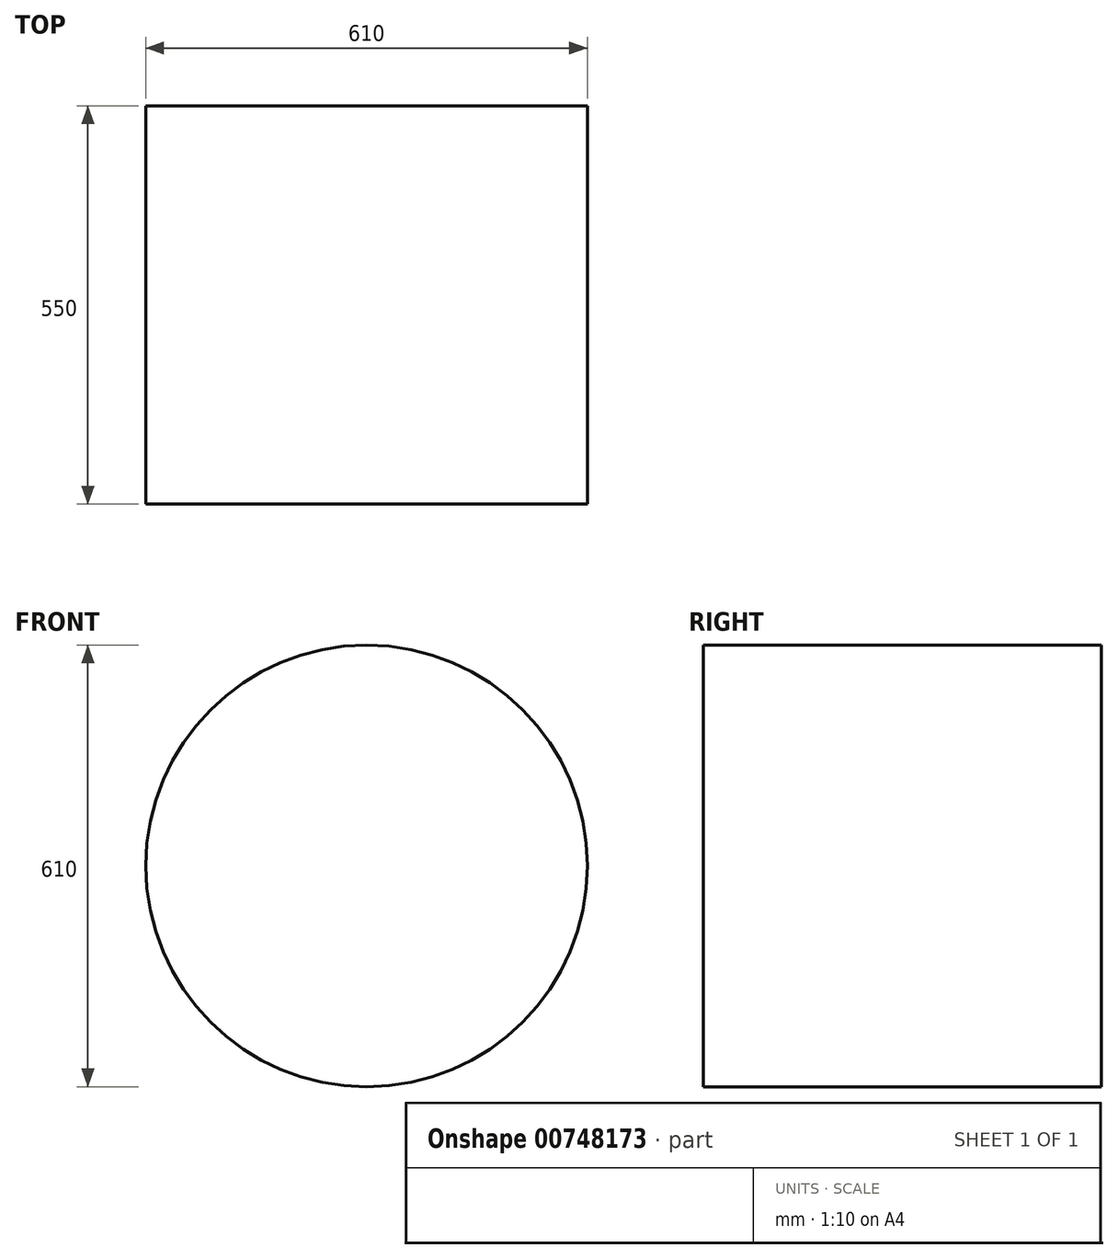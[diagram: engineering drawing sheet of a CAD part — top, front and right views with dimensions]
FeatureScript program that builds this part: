
annotation { "Feature Type Name" : "Feature", "Feature Type Description" : "" }
export const myFeature = defineFeature(function(context is Context, id is Id, definition is map)
    precondition{}
    {
        {
            var Q0;
            Q0=qCreatedBy(makeId("Front.planeOp"),FACE);
            var sketch = newSketch(context, id + "F0", { "sketchPlane" : qUnion([Q0])});
            skCircle(sketch, "E0", {"center": v(0, 0) * mm, "radius": 305 * mm});
            skSolve(sketch);
        }
        {
            var Q0;
            Q0=makeQuery(id+"F0.imprint","IMPRINT",FACE,{"disambiguationData":[TD([[makeQuery(id+"F0.imprint","IMPRINT",EDGE,{"derivedFrom":sQuery(id+"F0.wireOp",EDGE,"E0")}),1.0]])]});
            extrude(context, id + "F1", {"entities" : qUnion([Q0]), "depth" : 550 * mm, "offsetDistance" : 25 * mm});
        }
    });
